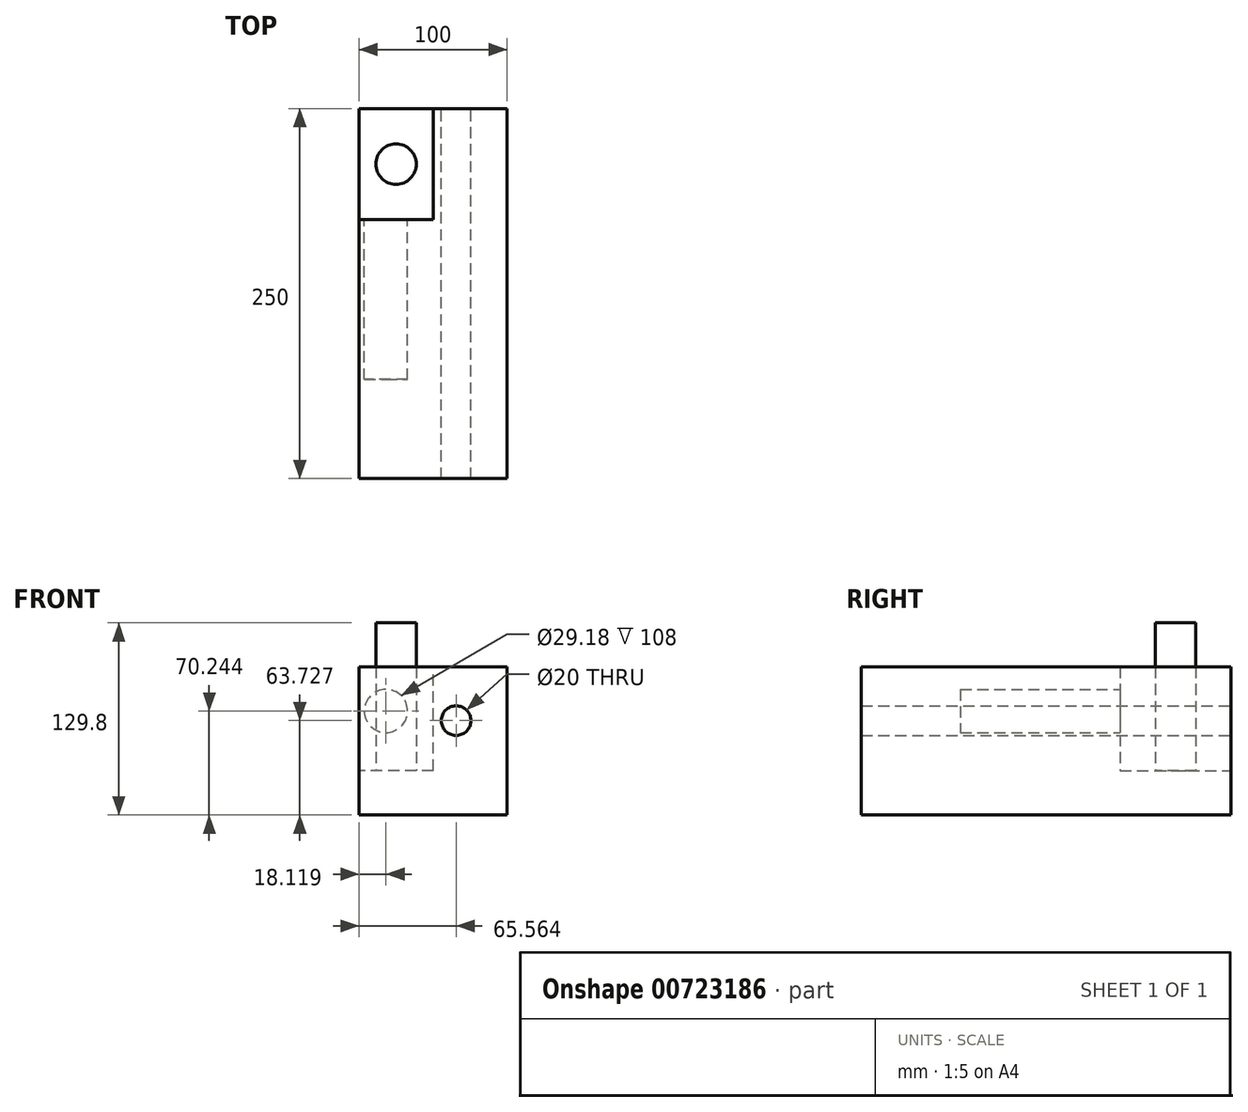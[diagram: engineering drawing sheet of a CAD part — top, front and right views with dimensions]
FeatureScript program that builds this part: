
annotation { "Feature Type Name" : "Feature", "Feature Type Description" : "" }
export const myFeature = defineFeature(function(context is Context, id is Id, definition is map)
    precondition{}
    {
        {
            var Q0;
            Q0=qCreatedBy(makeId("Top.planeOp"),FACE);
            var sketch = newSketch(context, id + "F0", { "sketchPlane" : qUnion([Q0])});
            skLineSegment(sketch, "E0.bottom", {"start": v(50, -125) * mm, "end": v(-50, -125) * mm});
            skLineSegment(sketch, "E0.top", {"start": v(50, 125) * mm, "end": v(-50, 125) * mm});
            skLineSegment(sketch, "E0.left", {"start": v(50, -125) * mm, "end": v(50, 125) * mm});
            skLineSegment(sketch, "E0.right", {"start": v(-50, -125) * mm, "end": v(-50, 125) * mm});
            skPoint(sketch, "E0.middle", {"position": v(0, 0) * mm});
            skSolve(sketch);
        }
        {
            var Q0;
            Q0=makeQuery(id+"F0.imprint","IMPRINT",FACE,{"disambiguationData":[TD([[makeQuery(id+"F0.imprint","IMPRINT",EDGE,{"derivedFrom":sQuery(id+"F0.wireOp",EDGE,"E0.bottom")}),-1.0]])]});
            var Q1;
            Q1 = qSketchRegion(id + "F0", true);
            extrude(context, id + "F1", {"entities" : qUnion([Q0, Q1]), "depth" : 100 * mm, "offsetDistance" : 25 * mm});
        }
        {
            var Q0;
            Q0=makeQuery(id+"F1.opExtrude","CAP_FACE",FACE,{"disambiguationData":[OSD([sQuery(id+"F0.wireOp",EDGE,"E0.bottom"),sQuery(id+"F0.wireOp",EDGE,"E0.top"),sQuery(id+"F0.wireOp",EDGE,"E0.left"),sQuery(id+"F0.wireOp",EDGE,"E0.right")])],"isStart":false});
            var sketch = newSketch(context, id + "F2", { "sketchPlane" : qUnion([Q0])});
            skLineSegment(sketch, "E1.bottom", {"start": v(0, 50) * mm, "end": v(-100, 50) * mm});
            skLineSegment(sketch, "E1.top", {"start": v(0, 200) * mm, "end": v(-100, 200) * mm});
            skLineSegment(sketch, "E1.left", {"start": v(0, 50) * mm, "end": v(0, 200) * mm});
            skLineSegment(sketch, "E1.right", {"start": v(-100, 50) * mm, "end": v(-100, 200) * mm});
            skPoint(sketch, "E1.middle", {"position": v(-50, 125) * mm});
            skSolve(sketch);
        }
        {
            var Q0;
            Q0 = qSketchRegion(id + "F2", true);
            extrude(context, id + "F3", {"entities" : qUnion([Q0]), "operationType" : NewBodyOperationType.REMOVE, "oppositeDirection" : true, "depth" : 70 * mm, "offsetDistance" : 25 * mm});
        }
        {
            var Q0;
            Q0=makeQuery(id+"F3.boolean.opBoolean","COPY",FACE,{"derivedFrom":makeQuery(id+"F3.opExtrude","SWEPT_FACE",FACE,{"disambiguationData":[OSD([sQuery(id+"F2.wireOp",EDGE,"E1.bottom")])]})});
            var sketch = newSketch(context, id + "F4", { "sketchPlane" : qUnion([Q0])});
            skCircle(sketch, "E2", {"center": v(31.88, 70.24) * mm, "radius": 14.6 * mm});
            skSolve(sketch);
        }
        {
            var Q0;
            Q0 = qSketchRegion(id + "F4", true);
            extrude(context, id + "F5", {"entities" : qUnion([Q0]), "operationType" : NewBodyOperationType.REMOVE, "oppositeDirection" : true, "depth" : 108 * mm, "offsetDistance" : 25 * mm});
        }
        {
            var Q0;
            Q0=makeQuery(id+"F1.opExtrude","SWEPT_FACE",FACE,{"disambiguationData":[OSD([sQuery(id+"F0.wireOp",EDGE,"E0.top")])]});
            var sketch = newSketch(context, id + "F6", { "sketchPlane" : qUnion([Q0])});
            skCircle(sketch, "E3", {"center": v(-15.56, 63.73) * mm, "radius": 19.98 * mm});
            skSolve(sketch);
        }
        {
            var Q0;
            Q0=sQuery(id+"F6.wireOp",VERTEX,"E3.center");
            var Q1;
            Q1=makeQuery(id+"F1.opExtrude","SWEPT_BODY",BODY,{"disambiguationData":[OSD([sQuery(id+"F0.wireOp",EDGE,"E0.bottom"),sQuery(id+"F0.wireOp",EDGE,"E0.top"),sQuery(id+"F0.wireOp",EDGE,"E0.left"),sQuery(id+"F0.wireOp",EDGE,"E0.right")])]});
            hole(context, id + "F7", {"style" : HoleStyle.SIMPLE, "endStyle" : HoleEndStyle.THROUGH, "holeDiameter" : 20 * mm, "majorDiameter" : 5 * mm, "isTappedThrough" : true, "tappedDepth" : 12 * mm, "tapClearance" : 3, "locations" : qUnion([Q0]), "scope" : qUnion([Q1])});
        }
        {
            var Q0;
            Q0=makeQuery(id+"F3.boolean.opBoolean","COPY",FACE,{"derivedFrom":makeQuery(id+"F3.opExtrude","CAP_FACE",FACE,{"disambiguationData":[OSD([sQuery(id+"F2.wireOp",EDGE,"E1.bottom"),sQuery(id+"F2.wireOp",EDGE,"E1.top"),sQuery(id+"F2.wireOp",EDGE,"E1.left"),sQuery(id+"F2.wireOp",EDGE,"E1.right")])],"isStart":false})});
            var sketch = newSketch(context, id + "F8", { "sketchPlane" : qUnion([Q0])});
            skLineSegment(sketch, "E4", {"start": v(0, 87.5) * mm, "end": v(-50, 87.5) * mm, "construction": true});
            skLineSegment(sketch, "E5", {"start": v(-25, 125) * mm, "end": v(-25, 50) * mm, "construction": true});
            skCircle(sketch, "E6", {"center": v(-25, 87.5) * mm, "radius": 13.65 * mm});
            skSolve(sketch);
        }
        {
            var Q0;
            Q0 = qSketchRegion(id + "F8", true);
            extrude(context, id + "F9", {"entities" : qUnion([Q0]), "depth" : 99.8 * mm, "offsetDistance" : 25 * mm});
        }
    });
